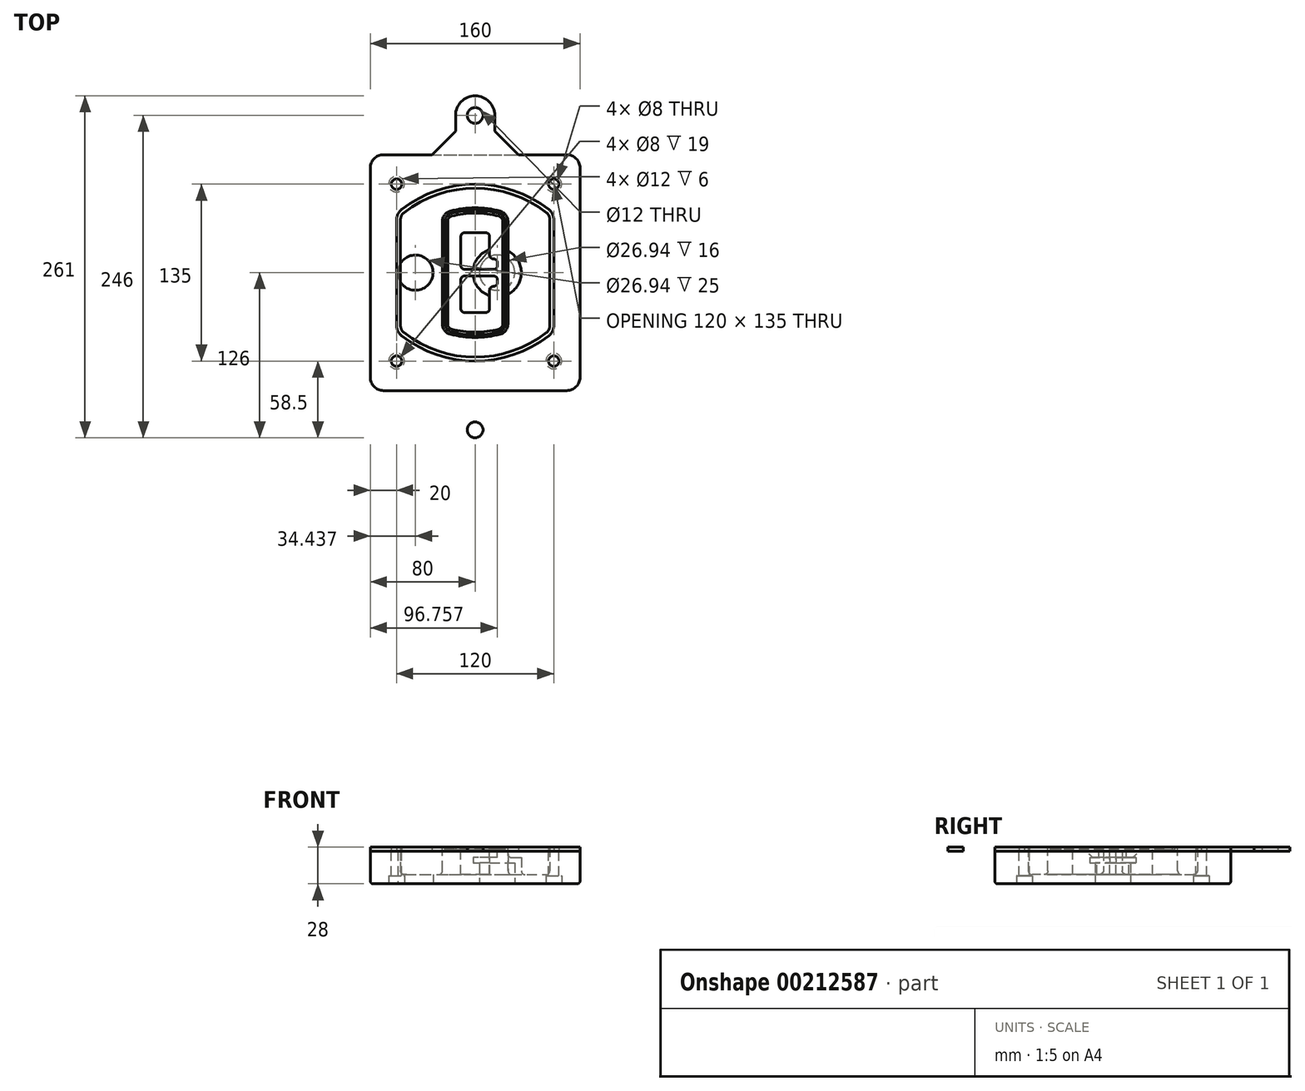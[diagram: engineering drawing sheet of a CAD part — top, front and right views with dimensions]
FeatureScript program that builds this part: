
annotation { "Feature Type Name" : "Feature", "Feature Type Description" : "" }
export const myFeature = defineFeature(function(context is Context, id is Id, definition is map)
    precondition{}
    {
        {
            var Q0;
            Q0=qCreatedBy(makeId("Top.planeOp"),FACE);
            var sketch = newSketch(context, id + "F0", { "sketchPlane" : qUnion([Q0])});
            skPoint(sketch, "E0.rect.middle", {"position": v(0, 0) * mm});
            skLineSegment(sketch, "E1.bottom", {"start": v(-70, -90) * mm, "end": v(70, -90) * mm});
            skLineSegment(sketch, "E1.top", {"start": v(-70, 90) * mm, "end": v(70, 90) * mm});
            skLineSegment(sketch, "E1.left", {"start": v(-80, -80) * mm, "end": v(-80, 80) * mm});
            skLineSegment(sketch, "E1.right", {"start": v(80, -80) * mm, "end": v(80, 80) * mm});
            skLineSegment(sketch, "E2", {"start": v(-80, 90) * mm, "end": v(80, -90) * mm, "construction": true});
            skLineSegment(sketch, "E3", {"start": v(80, 90) * mm, "end": v(-80, -90) * mm, "construction": true});
            skCircle(sketch, "E4", {"center": v(-60, 67.5) * mm, "radius": 4 * mm});
            skCircle(sketch, "E5", {"center": v(60, 67.5) * mm, "radius": 4 * mm});
            skCircle(sketch, "E6", {"center": v(60, -67.5) * mm, "radius": 4 * mm});
            skCircle(sketch, "E7", {"center": v(-60, -67.5) * mm, "radius": 4 * mm});
            skLineSegment(sketch, "E8", {"start": v(-60, 67.5) * mm, "end": v(60, 67.5) * mm, "construction": true});
            skLineSegment(sketch, "E9", {"start": v(60, 67.5) * mm, "end": v(60, -67.5) * mm, "construction": true});
            skLineSegment(sketch, "E10", {"start": v(60, -67.5) * mm, "end": v(-60, -67.5) * mm, "construction": true});
            skLineSegment(sketch, "E11", {"start": v(-60, -67.5) * mm, "end": v(-60, 67.5) * mm, "construction": true});
            skLineSegment(sketch, "E12", {"start": v(-60, 40.3) * mm, "end": v(-60, -40.3) * mm});
            skLineSegment(sketch, "E13", {"start": v(60, 40.3) * mm, "end": v(60, -40.3) * mm});
            skArc(sketch, "E14", {"start": v(56.15, 48.18) * mm, "mid": v(0, 67.5) * mm, "end": v(-56.15, 48.18) * mm});
            skArc(sketch, "E15", {"start": v(-56.15, -48.18) * mm, "mid": v(0, -67.5) * mm, "end": v(56.15, -48.18) * mm});
            skLineSegment(sketch, "E16", {"start": v(-60, 0) * mm, "end": v(60, 0) * mm, "construction": true});
            skPoint(sketch, "E17.visualSharp", {"position": v(-60, -45) * mm});
            skArc(sketch, "E17.filletArc", {"start": v(-60, -40.3) * mm, "mid": v(-58.99, -44.68) * mm, "end": v(-56.15, -48.18) * mm});
            skPoint(sketch, "E18.visualSharp", {"position": v(-60, 45) * mm});
            skArc(sketch, "E18.filletArc", {"start": v(-56.15, 48.18) * mm, "mid": v(-58.99, 44.68) * mm, "end": v(-60, 40.3) * mm});
            skPoint(sketch, "E19.visualSharp", {"position": v(60, 45) * mm});
            skArc(sketch, "E19.filletArc", {"start": v(60, 40.3) * mm, "mid": v(58.99, 44.68) * mm, "end": v(56.15, 48.18) * mm});
            skPoint(sketch, "E20.visualSharp", {"position": v(60, -45) * mm});
            skArc(sketch, "E20.filletArc", {"start": v(56.15, -48.18) * mm, "mid": v(58.99, -44.68) * mm, "end": v(60, -40.3) * mm});
            skPoint(sketch, "E21.visualSharp", {"position": v(-80, 90) * mm});
            skArc(sketch, "E21.filletArc", {"start": v(-70, 90) * mm, "mid": v(-77.07, 87.07) * mm, "end": v(-80, 80) * mm});
            skPoint(sketch, "E22.visualSharp", {"position": v(80, 90) * mm});
            skArc(sketch, "E22.filletArc", {"start": v(80, 80) * mm, "mid": v(77.07, 87.07) * mm, "end": v(70, 90) * mm});
            skPoint(sketch, "E23.visualSharp", {"position": v(80, -90) * mm});
            skArc(sketch, "E23.filletArc", {"start": v(70, -90) * mm, "mid": v(77.07, -87.07) * mm, "end": v(80, -80) * mm});
            skPoint(sketch, "E24.visualSharp", {"position": v(-80, -90) * mm});
            skArc(sketch, "E24.filletArc", {"start": v(-80, -80) * mm, "mid": v(-77.07, -87.07) * mm, "end": v(-70, -90) * mm});
            skArc(sketch, "E25.0", {"start": v(57, 40.3) * mm, "mid": v(56.3, 43.36) * mm, "end": v(54.3, 45.81) * mm});
            skLineSegment(sketch, "E25.1", {"start": v(57, 40.3) * mm, "end": v(57, -40.3) * mm});
            skArc(sketch, "E25.2", {"start": v(54.3, -45.81) * mm, "mid": v(56.3, -43.36) * mm, "end": v(57, -40.3) * mm});
            skArc(sketch, "E25.3", {"start": v(-54.3, -45.81) * mm, "mid": v(0, -64.5) * mm, "end": v(54.3, -45.81) * mm});
            skArc(sketch, "E25.4", {"start": v(-57, -40.3) * mm, "mid": v(-56.3, -43.36) * mm, "end": v(-54.3, -45.81) * mm});
            skArc(sketch, "E25.5", {"start": v(54.3, 45.81) * mm, "mid": v(0, 64.5) * mm, "end": v(-54.3, 45.81) * mm});
            skLineSegment(sketch, "E25.6", {"start": v(-57, 40.3) * mm, "end": v(-57, -40.3) * mm});
            skArc(sketch, "E25.7", {"start": v(-54.3, 45.81) * mm, "mid": v(-56.3, 43.36) * mm, "end": v(-57, 40.3) * mm});
            skArc(sketch, "E26.0", {"start": v(-58.62, 51.33) * mm, "mid": v(-62.58, 46.43) * mm, "end": v(-64, 40.3) * mm});
            skArc(sketch, "E26.1", {"start": v(58.62, 51.33) * mm, "mid": v(0, 71.5) * mm, "end": v(-58.62, 51.33) * mm});
            skArc(sketch, "E26.2", {"start": v(64, 40.3) * mm, "mid": v(62.58, 46.43) * mm, "end": v(58.62, 51.33) * mm});
            skLineSegment(sketch, "E26.3", {"start": v(64, 40.3) * mm, "end": v(64, -40.3) * mm});
            skArc(sketch, "E26.4", {"start": v(58.62, -51.33) * mm, "mid": v(62.58, -46.43) * mm, "end": v(64, -40.3) * mm});
            skLineSegment(sketch, "E26.5", {"start": v(-64, 40.3) * mm, "end": v(-64, -40.3) * mm});
            skArc(sketch, "E26.6", {"start": v(-58.62, -51.33) * mm, "mid": v(0, -71.5) * mm, "end": v(58.62, -51.33) * mm});
            skArc(sketch, "E26.7", {"start": v(-64, -40.3) * mm, "mid": v(-62.58, -46.43) * mm, "end": v(-58.62, -51.33) * mm});
            skSolve(sketch);
        }
        {
            var Q0;
            Q0=makeQuery(id+"F0.imprint","IMPRINT",FACE,{"disambiguationData":[TD([[makeQuery(id+"F0.imprint","IMPRINT",EDGE,{"derivedFrom":sQuery(id+"F0.wireOp",EDGE,"E1.bottom")}),1.0]])]});
            var Q1;
            Q1=makeQuery(id+"F0.imprint","IMPRINT",FACE,{"disambiguationData":[TD([[makeQuery(id+"F0.imprint","IMPRINT",EDGE,{"derivedFrom":sQuery(id+"F0.wireOp",EDGE,"E12")}),1.0]])]});
            var Q2;
            Q2=makeQuery(id+"F0.imprint","IMPRINT",FACE,{"disambiguationData":[TD([[makeQuery(id+"F0.imprint","IMPRINT",EDGE,{"derivedFrom":sQuery(id+"F0.wireOp",EDGE,"E25.0")}),1.0]])]});
            var Q3;
            Q3=makeQuery(id+"F0.imprint","IMPRINT",FACE,{"disambiguationData":[TD([[makeQuery(id+"F0.imprint","IMPRINT",EDGE,{"derivedFrom":sQuery(id+"F0.wireOp",EDGE,"E12")}),-1.0]])]});
            extrude(context, id + "F1", {"entities" : qUnion([Q0, Q1, Q2, Q3]), "oppositeDirection" : true, "depth" : 25 * mm});
        }
        {
            var Q0;
            Q0=makeQuery(id+"F0.imprint","IMPRINT",FACE,{"disambiguationData":[TD([[makeQuery(id+"F0.imprint","IMPRINT",EDGE,{"derivedFrom":sQuery(id+"F0.wireOp",EDGE,"E12")}),1.0]])]});
            extrude(context, id + "F2", {"entities" : qUnion([Q0]), "operationType" : NewBodyOperationType.ADD, "depth" : 3 * mm});
        }
        {
            var Q0;
            Q0=makeQuery(id+"F0.imprint","IMPRINT",FACE,{"disambiguationData":[TD([[makeQuery(id+"F0.imprint","IMPRINT",EDGE,{"derivedFrom":sQuery(id+"F0.wireOp",EDGE,"E25.0")}),1.0]])]});
            extrude(context, id + "F3", {"entities" : qUnion([Q0]), "operationType" : NewBodyOperationType.REMOVE, "oppositeDirection" : true, "depth" : 18 * mm});
        }
        {
            var Q0;
            Q0=makeQuery(id+"F2.opExtrude","CAP_FACE",FACE,{"disambiguationData":[OSD([sQuery(id+"F0.wireOp",EDGE,"E12"),sQuery(id+"F0.wireOp",EDGE,"E13"),sQuery(id+"F0.wireOp",EDGE,"E14"),sQuery(id+"F0.wireOp",EDGE,"E15"),sQuery(id+"F0.wireOp",EDGE,"E17.filletArc"),sQuery(id+"F0.wireOp",EDGE,"E18.filletArc"),sQuery(id+"F0.wireOp",EDGE,"E19.filletArc"),sQuery(id+"F0.wireOp",EDGE,"E20.filletArc"),sQuery(id+"F0.wireOp",EDGE,"E25.0"),sQuery(id+"F0.wireOp",EDGE,"E25.1"),sQuery(id+"F0.wireOp",EDGE,"E25.2"),sQuery(id+"F0.wireOp",EDGE,"E25.3"),sQuery(id+"F0.wireOp",EDGE,"E25.4"),sQuery(id+"F0.wireOp",EDGE,"E25.5"),sQuery(id+"F0.wireOp",EDGE,"E25.6"),sQuery(id+"F0.wireOp",EDGE,"E25.7")])],"isStart":false});
            var sketch = newSketch(context, id + "F4", { "sketchPlane" : qUnion([Q0])});
            skArc(sketch, "E27.0", {"start": v(-19.08, -46.97) * mm, "mid": v(0, -49.5) * mm, "end": v(19.08, -46.97) * mm});
            skArc(sketch, "E28.0", {"start": v(19.08, 46.97) * mm, "mid": v(0, 49.5) * mm, "end": v(-19.08, 46.97) * mm});
            skLineSegment(sketch, "E29", {"start": v(-25, 39.25) * mm, "end": v(-25, -39.25) * mm});
            skLineSegment(sketch, "E30", {"start": v(25, 39.25) * mm, "end": v(25, -39.25) * mm});
            skLineSegment(sketch, "E31", {"start": v(-25, 45.1) * mm, "end": v(25, 45.1) * mm, "construction": true});
            skLineSegment(sketch, "E32", {"start": v(-25, -45.1) * mm, "end": v(25, -45.1) * mm, "construction": true});
            skPoint(sketch, "E33.visualSharp", {"position": v(-25, 45.1) * mm});
            skArc(sketch, "E33.filletArc", {"start": v(-19.08, 46.97) * mm, "mid": v(-23.35, 44.11) * mm, "end": v(-25, 39.25) * mm});
            skPoint(sketch, "E34.visualSharp", {"position": v(25, 45.1) * mm});
            skArc(sketch, "E34.filletArc", {"start": v(25, 39.25) * mm, "mid": v(23.35, 44.11) * mm, "end": v(19.08, 46.97) * mm});
            skPoint(sketch, "E35.visualSharp", {"position": v(25, -45.1) * mm});
            skArc(sketch, "E35.filletArc", {"start": v(19.08, -46.97) * mm, "mid": v(23.35, -44.11) * mm, "end": v(25, -39.25) * mm});
            skPoint(sketch, "E36.visualSharp", {"position": v(-25, -45.1) * mm});
            skArc(sketch, "E36.filletArc", {"start": v(-25, -39.25) * mm, "mid": v(-23.35, -44.11) * mm, "end": v(-19.08, -46.97) * mm});
            skArc(sketch, "E37.0", {"start": v(54.3, 45.81) * mm, "mid": v(0, 64.5) * mm, "end": v(-54.3, 45.81) * mm});
            skArc(sketch, "E37.1", {"start": v(-54.3, 45.81) * mm, "mid": v(-56.3, 43.36) * mm, "end": v(-57, 40.3) * mm});
            skLineSegment(sketch, "E37.2", {"start": v(-57, 40.3) * mm, "end": v(-57, -40.3) * mm});
            skArc(sketch, "E37.3", {"start": v(-57, -40.3) * mm, "mid": v(-56.3, -43.36) * mm, "end": v(-54.3, -45.81) * mm});
            skArc(sketch, "E37.4", {"start": v(-54.3, -45.81) * mm, "mid": v(0, -64.5) * mm, "end": v(54.3, -45.81) * mm});
            skArc(sketch, "E37.5", {"start": v(54.3, -45.81) * mm, "mid": v(56.3, -43.36) * mm, "end": v(57, -40.3) * mm});
            skLineSegment(sketch, "E37.6", {"start": v(57, 40.3) * mm, "end": v(57, -40.3) * mm});
            skArc(sketch, "E37.7", {"start": v(57, 40.3) * mm, "mid": v(56.3, 43.36) * mm, "end": v(54.3, 45.81) * mm});
            skLineSegment(sketch, "E38.0", {"start": v(23, 39.25) * mm, "end": v(23, -39.25) * mm});
            skArc(sketch, "E38.1", {"start": v(18.56, -45.04) * mm, "mid": v(21.76, -42.9) * mm, "end": v(23, -39.25) * mm});
            skArc(sketch, "E38.2", {"start": v(-18.56, -45.04) * mm, "mid": v(0, -47.5) * mm, "end": v(18.56, -45.04) * mm});
            skArc(sketch, "E38.3", {"start": v(-23, -39.25) * mm, "mid": v(-21.76, -42.9) * mm, "end": v(-18.56, -45.04) * mm});
            skLineSegment(sketch, "E38.4", {"start": v(-23, 39.25) * mm, "end": v(-23, -39.25) * mm});
            skArc(sketch, "E38.5", {"start": v(23, 39.25) * mm, "mid": v(21.76, 42.9) * mm, "end": v(18.56, 45.04) * mm});
            skArc(sketch, "E38.6", {"start": v(-18.56, 45.04) * mm, "mid": v(-21.76, 42.9) * mm, "end": v(-23, 39.25) * mm});
            skArc(sketch, "E38.7", {"start": v(18.56, 45.04) * mm, "mid": v(0, 47.5) * mm, "end": v(-18.56, 45.04) * mm});
            skArc(sketch, "E39.0", {"start": v(21, 39.25) * mm, "mid": v(20.18, 41.68) * mm, "end": v(18.04, 43.1) * mm});
            skLineSegment(sketch, "E39.1", {"start": v(21, 39.25) * mm, "end": v(21, -39.25) * mm});
            skArc(sketch, "E39.2", {"start": v(18.04, -43.1) * mm, "mid": v(20.18, -41.68) * mm, "end": v(21, -39.25) * mm});
            skArc(sketch, "E39.3", {"start": v(-18.04, -43.1) * mm, "mid": v(0, -45.5) * mm, "end": v(18.04, -43.1) * mm});
            skArc(sketch, "E39.4", {"start": v(-21, -39.25) * mm, "mid": v(-20.18, -41.68) * mm, "end": v(-18.04, -43.1) * mm});
            skArc(sketch, "E39.5", {"start": v(18.04, 43.1) * mm, "mid": v(0, 45.5) * mm, "end": v(-18.04, 43.1) * mm});
            skLineSegment(sketch, "E39.6", {"start": v(-21, 39.25) * mm, "end": v(-21, -39.25) * mm});
            skArc(sketch, "E39.7", {"start": v(-18.04, 43.1) * mm, "mid": v(-20.18, 41.68) * mm, "end": v(-21, 39.25) * mm});
            skLineSegment(sketch, "E40", {"start": v(-25, 0) * mm, "end": v(25, 0) * mm, "construction": true});
            skLineSegment(sketch, "E41", {"start": v(-11, 5.5) * mm, "end": v(-11, 27.5) * mm});
            skLineSegment(sketch, "E42", {"start": v(-8, 30.5) * mm, "end": v(8, 30.5) * mm});
            skLineSegment(sketch, "E43", {"start": v(11, 27.5) * mm, "end": v(11, 13.5) * mm});
            skLineSegment(sketch, "E44", {"start": v(14, 10.5) * mm, "end": v(14, 10.5) * mm});
            skLineSegment(sketch, "E45", {"start": v(17, 7.5) * mm, "end": v(17, 5.5) * mm});
            skLineSegment(sketch, "E46", {"start": v(14, 2.5) * mm, "end": v(-8, 2.5) * mm});
            skPoint(sketch, "E47.visualSharp", {"position": v(-11, 30.5) * mm});
            skArc(sketch, "E47.filletArc", {"start": v(-8, 30.5) * mm, "mid": v(-10.12, 29.62) * mm, "end": v(-11, 27.5) * mm});
            skPoint(sketch, "E48.visualSharp", {"position": v(11, 30.5) * mm});
            skArc(sketch, "E48.filletArc", {"start": v(11, 27.5) * mm, "mid": v(10.12, 29.62) * mm, "end": v(8, 30.5) * mm});
            skPoint(sketch, "E49.visualSharp", {"position": v(11, 10.5) * mm});
            skArc(sketch, "E49.filletArc", {"start": v(11, 13.5) * mm, "mid": v(11.88, 11.38) * mm, "end": v(14, 10.5) * mm});
            skPoint(sketch, "E50.visualSharp", {"position": v(17, 10.5) * mm});
            skArc(sketch, "E50.filletArc", {"start": v(17, 7.5) * mm, "mid": v(16.12, 9.62) * mm, "end": v(14, 10.5) * mm});
            skPoint(sketch, "E51.visualSharp", {"position": v(17, 2.5) * mm});
            skArc(sketch, "E51.filletArc", {"start": v(14, 2.5) * mm, "mid": v(16.12, 3.38) * mm, "end": v(17, 5.5) * mm});
            skPoint(sketch, "E52.visualSharp", {"position": v(-11, 2.5) * mm});
            skArc(sketch, "E52.filletArc", {"start": v(-11, 5.5) * mm, "mid": v(-10.12, 3.38) * mm, "end": v(-8, 2.5) * mm});
            skLineSegment(sketch, "E53.0.MirrorCS", {"start": v(14, -2.5) * mm, "end": v(-8, -2.5) * mm});
            skArc(sketch, "E54.0.MirrorCS", {"start": v(-11, -5.5) * mm, "mid": v(-10.12, -3.38) * mm, "end": v(-8, -2.5) * mm});
            skLineSegment(sketch, "E55.0.MirrorCS", {"start": v(-11, -5.5) * mm, "end": v(-11, -27.5) * mm});
            skArc(sketch, "E56.0.MirrorCS", {"start": v(-8, -30.5) * mm, "mid": v(-10.12, -29.62) * mm, "end": v(-11, -27.5) * mm});
            skLineSegment(sketch, "E57.0.MirrorCS", {"start": v(-8, -30.5) * mm, "end": v(8, -30.5) * mm});
            skArc(sketch, "E58.0.MirrorCS", {"start": v(11, -27.5) * mm, "mid": v(10.12, -29.62) * mm, "end": v(8, -30.5) * mm});
            skLineSegment(sketch, "E59.0.MirrorCS", {"start": v(11, -27.5) * mm, "end": v(11, -13.5) * mm});
            skArc(sketch, "E60.0.MirrorCS", {"start": v(11, -13.5) * mm, "mid": v(11.88, -11.38) * mm, "end": v(14, -10.5) * mm});
            skArc(sketch, "E61.0.MirrorCS", {"start": v(17, -7.5) * mm, "mid": v(16.12, -9.62) * mm, "end": v(14, -10.5) * mm});
            skLineSegment(sketch, "E62.0.MirrorCS", {"start": v(17, -7.5) * mm, "end": v(17, -5.5) * mm});
            skArc(sketch, "E63.0.MirrorCS", {"start": v(14, -2.5) * mm, "mid": v(16.12, -3.38) * mm, "end": v(17, -5.5) * mm});
            skSolve(sketch);
        }
        {
            var Q0;
            Q0=makeQuery(id+"F4.imprint","IMPRINT",FACE,{"disambiguationData":[TD([[makeQuery(id+"F4.imprint","IMPRINT",EDGE,{"derivedFrom":sQuery(id+"F4.wireOp",EDGE,"E27.0")}),1.0]])]});
            var Q1;
            Q1=makeQuery(id+"F4.imprint","IMPRINT",FACE,{"disambiguationData":[TD([[makeQuery(id+"F4.imprint","IMPRINT",EDGE,{"derivedFrom":sQuery(id+"F4.wireOp",EDGE,"E38.0")}),-1.0]])]});
            var Q2;
            Q2=makeQuery(id+"F4.imprint","IMPRINT",FACE,{"disambiguationData":[TD([[makeQuery(id+"F4.imprint","IMPRINT",EDGE,{"derivedFrom":sQuery(id+"F4.wireOp",EDGE,"E39.0")}),1.0]])]});
            extrude(context, id + "F5", {"entities" : qUnion([Q0, Q1, Q2]), "operationType" : NewBodyOperationType.ADD, "endBound" : BoundingType.UP_TO_NEXT, "oppositeDirection" : true, "depth" : 25 * mm});
        }
        {
            var Q0;
            Q0=makeQuery(id+"F4.imprint","IMPRINT",FACE,{"disambiguationData":[TD([[makeQuery(id+"F4.imprint","IMPRINT",EDGE,{"derivedFrom":sQuery(id+"F4.wireOp",EDGE,"E38.0")}),-1.0]])]});
            extrude(context, id + "F6", {"entities" : qUnion([Q0]), "operationType" : NewBodyOperationType.REMOVE, "oppositeDirection" : true, "depth" : 2 * mm});
        }
        {
            var Q0;
            Q0=makeQuery(id+"F1.opExtrude","CAP_FACE",FACE,{"disambiguationData":[OSD([sQuery(id+"F0.wireOp",EDGE,"E1.bottom"),sQuery(id+"F0.wireOp",EDGE,"E1.top"),sQuery(id+"F0.wireOp",EDGE,"E1.left"),sQuery(id+"F0.wireOp",EDGE,"E1.right"),sQuery(id+"F0.wireOp",EDGE,"E4"),sQuery(id+"F0.wireOp",EDGE,"E5"),sQuery(id+"F0.wireOp",EDGE,"E6"),sQuery(id+"F0.wireOp",EDGE,"E7"),sQuery(id+"F0.wireOp",EDGE,"E21.filletArc"),sQuery(id+"F0.wireOp",EDGE,"E22.filletArc"),sQuery(id+"F0.wireOp",EDGE,"E23.filletArc"),sQuery(id+"F0.wireOp",EDGE,"E24.filletArc")])],"isStart":false});
            var sketch = newSketch(context, id + "F7", { "sketchPlane" : qUnion([Q0])});
            skCircle(sketch, "E64", {"center": v(16.76, 0) * mm, "radius": 13.47 * mm});
            skCircle(sketch, "E65", {"center": v(-45.56, 0) * mm, "radius": 13.47 * mm});
            skLineSegment(sketch, "E66", {"start": v(80, 0) * mm, "end": v(-80, 0) * mm});
            skCircle(sketch, "E67", {"center": v(16.76, 0) * mm, "radius": 18.47 * mm});
            skCircle(sketch, "E68", {"center": v(60, -67.5) * mm, "radius": 6 * mm});
            skCircle(sketch, "E69", {"center": v(-60, -67.5) * mm, "radius": 6 * mm});
            skCircle(sketch, "E70", {"center": v(-60, 67.5) * mm, "radius": 6 * mm});
            skCircle(sketch, "E71", {"center": v(60, 67.5) * mm, "radius": 6 * mm});
            skSolve(sketch);
        }
        {
            var Q0;
            {var subQ1=sQuery(id+"F7.wireOp",EDGE,"E66");var subQ4=sQuery(id+"F7.wireOp",EDGE,"E64");var subQ6=makeQuery(id+"F7.imprint","INTERSECT",VERTEX,{"disambiguationData":[OD(0.0)],"derivedFrom":[subQ4,subQ1]});Q0=makeQuery(id+"F7.imprint","IMPRINT",FACE,{"disambiguationData":[TD([[makeQuery(id+"F7.imprint","IMPRINT",EDGE,{"disambiguationData":[TD([[subQ6,-1.0]])],"derivedFrom":subQ4}),-1.0]])]});}
            var Q1;
            {var subQ0=sQuery(id+"F7.wireOp",EDGE,"E66");var subQ1=sQuery(id+"F7.wireOp",EDGE,"E64");var subQ3=makeQuery(id+"F7.imprint","INTERSECT",VERTEX,{"disambiguationData":[OD(0.0)],"derivedFrom":[subQ1,subQ0]});Q1=makeQuery(id+"F7.imprint","IMPRINT",FACE,{"disambiguationData":[TD([[makeQuery(id+"F7.imprint","IMPRINT",EDGE,{"disambiguationData":[TD([[subQ3,-1.0]])],"derivedFrom":subQ1}),1.0]])]});}
            var Q2;
            {var subQ0=sQuery(id+"F7.wireOp",EDGE,"E66");var subQ1=sQuery(id+"F7.wireOp",EDGE,"E64");var subQ3=makeQuery(id+"F7.imprint","INTERSECT",VERTEX,{"disambiguationData":[OD(0.0)],"derivedFrom":[subQ1,subQ0]});Q2=makeQuery(id+"F7.imprint","IMPRINT",FACE,{"disambiguationData":[TD([[makeQuery(id+"F7.imprint","IMPRINT",EDGE,{"disambiguationData":[TD([[subQ3,1.0]])],"derivedFrom":subQ1}),1.0]])]});}
            var Q3;
            {var subQ1=sQuery(id+"F7.wireOp",EDGE,"E66");var subQ4=sQuery(id+"F7.wireOp",EDGE,"E64");var subQ6=makeQuery(id+"F7.imprint","INTERSECT",VERTEX,{"disambiguationData":[OD(0.0)],"derivedFrom":[subQ4,subQ1]});Q3=makeQuery(id+"F7.imprint","IMPRINT",FACE,{"disambiguationData":[TD([[makeQuery(id+"F7.imprint","IMPRINT",EDGE,{"disambiguationData":[TD([[subQ6,1.0]])],"derivedFrom":subQ4}),-1.0]])]});}
            extrude(context, id + "F8", {"entities" : qUnion([Q0, Q1, Q2, Q3]), "operationType" : NewBodyOperationType.ADD, "oppositeDirection" : true, "depth" : 20 * mm});
        }
        {
            var Q0;
            {var subQ0=sQuery(id+"F7.wireOp",EDGE,"E66");var subQ1=sQuery(id+"F7.wireOp",EDGE,"E64");var subQ3=makeQuery(id+"F7.imprint","INTERSECT",VERTEX,{"disambiguationData":[OD(0.0)],"derivedFrom":[subQ1,subQ0]});Q0=makeQuery(id+"F7.imprint","IMPRINT",FACE,{"disambiguationData":[TD([[makeQuery(id+"F7.imprint","IMPRINT",EDGE,{"disambiguationData":[TD([[subQ3,-1.0]])],"derivedFrom":subQ1}),1.0]])]});}
            var Q1;
            {var subQ0=sQuery(id+"F7.wireOp",EDGE,"E66");var subQ1=sQuery(id+"F7.wireOp",EDGE,"E64");var subQ3=makeQuery(id+"F7.imprint","INTERSECT",VERTEX,{"disambiguationData":[OD(0.0)],"derivedFrom":[subQ1,subQ0]});Q1=makeQuery(id+"F7.imprint","IMPRINT",FACE,{"disambiguationData":[TD([[makeQuery(id+"F7.imprint","IMPRINT",EDGE,{"disambiguationData":[TD([[subQ3,1.0]])],"derivedFrom":subQ1}),1.0]])]});}
            extrude(context, id + "F9", {"entities" : qUnion([Q0, Q1]), "operationType" : NewBodyOperationType.REMOVE, "oppositeDirection" : true, "depth" : 16 * mm});
        }
        {
            var Q0;
            {var subQ0=sQuery(id+"F7.wireOp",EDGE,"E66");var subQ1=sQuery(id+"F7.wireOp",EDGE,"E65");var subQ3=makeQuery(id+"F7.imprint","INTERSECT",VERTEX,{"disambiguationData":[OD(0.0)],"derivedFrom":[subQ1,subQ0]});Q0=makeQuery(id+"F7.imprint","IMPRINT",FACE,{"disambiguationData":[TD([[makeQuery(id+"F7.imprint","IMPRINT",EDGE,{"disambiguationData":[TD([[subQ3,-1.0]])],"derivedFrom":subQ1}),1.0]])]});}
            var Q1;
            {var subQ0=sQuery(id+"F7.wireOp",EDGE,"E66");var subQ1=sQuery(id+"F7.wireOp",EDGE,"E65");var subQ3=makeQuery(id+"F7.imprint","INTERSECT",VERTEX,{"disambiguationData":[OD(0.0)],"derivedFrom":[subQ1,subQ0]});Q1=makeQuery(id+"F7.imprint","IMPRINT",FACE,{"disambiguationData":[TD([[makeQuery(id+"F7.imprint","IMPRINT",EDGE,{"disambiguationData":[TD([[subQ3,1.0]])],"derivedFrom":subQ1}),1.0]])]});}
            extrude(context, id + "F10", {"entities" : qUnion([Q0, Q1]), "operationType" : NewBodyOperationType.REMOVE, "oppositeDirection" : true, "depth" : 25 * mm});
        }
        {
            var Q0;
            Q0=makeQuery(id+"F7.imprint","IMPRINT",FACE,{"disambiguationData":[TD([[makeQuery(id+"F7.imprint","IMPRINT",EDGE,{"derivedFrom":sQuery(id+"F7.wireOp",EDGE,"E68")}),1.0]])]});
            var Q1;
            Q1=makeQuery(id+"F7.imprint","IMPRINT",FACE,{"disambiguationData":[TD([[makeQuery(id+"F7.imprint","IMPRINT",EDGE,{"derivedFrom":makeQuery(id+"F1.opExtrude","CAP_EDGE",EDGE,{"disambiguationData":[OSD([sQuery(id+"F0.wireOp",EDGE,"E5")])],"isStart":false})}),-1.0]])]});
            var Q2;
            Q2=makeQuery(id+"F7.imprint","IMPRINT",FACE,{"disambiguationData":[TD([[makeQuery(id+"F7.imprint","IMPRINT",EDGE,{"derivedFrom":sQuery(id+"F7.wireOp",EDGE,"E69")}),1.0]])]});
            var Q3;
            Q3=makeQuery(id+"F7.imprint","IMPRINT",FACE,{"disambiguationData":[TD([[makeQuery(id+"F7.imprint","IMPRINT",EDGE,{"derivedFrom":makeQuery(id+"F1.opExtrude","CAP_EDGE",EDGE,{"disambiguationData":[OSD([sQuery(id+"F0.wireOp",EDGE,"E4")])],"isStart":false})}),-1.0]])]});
            var Q4;
            Q4=makeQuery(id+"F7.imprint","IMPRINT",FACE,{"disambiguationData":[TD([[makeQuery(id+"F7.imprint","IMPRINT",EDGE,{"derivedFrom":sQuery(id+"F7.wireOp",EDGE,"E70")}),1.0]])]});
            var Q5;
            Q5=makeQuery(id+"F7.imprint","IMPRINT",FACE,{"disambiguationData":[TD([[makeQuery(id+"F7.imprint","IMPRINT",EDGE,{"derivedFrom":makeQuery(id+"F1.opExtrude","CAP_EDGE",EDGE,{"disambiguationData":[OSD([sQuery(id+"F0.wireOp",EDGE,"E7")])],"isStart":false})}),-1.0]])]});
            var Q6;
            Q6=makeQuery(id+"F7.imprint","IMPRINT",FACE,{"disambiguationData":[TD([[makeQuery(id+"F7.imprint","IMPRINT",EDGE,{"derivedFrom":sQuery(id+"F7.wireOp",EDGE,"E71")}),1.0]])]});
            var Q7;
            Q7=makeQuery(id+"F7.imprint","IMPRINT",FACE,{"disambiguationData":[TD([[makeQuery(id+"F7.imprint","IMPRINT",EDGE,{"derivedFrom":makeQuery(id+"F1.opExtrude","CAP_EDGE",EDGE,{"disambiguationData":[OSD([sQuery(id+"F0.wireOp",EDGE,"E6")])],"isStart":false})}),-1.0]])]});
            extrude(context, id + "F11", {"entities" : qUnion([Q0, Q1, Q2, Q3, Q4, Q5, Q6, Q7]), "operationType" : NewBodyOperationType.REMOVE, "oppositeDirection" : true, "depth" : 6 * mm});
        }
        {
            var Q0;
            Q0=makeQuery(id+"F9.boolean.opBoolean","COPY",FACE,{"derivedFrom":makeQuery(id+"F9.opExtrude","CAP_FACE",FACE,{"disambiguationData":[OSD([sQuery(id+"F7.wireOp",EDGE,"E64")])],"isStart":false})});
            var sketch = newSketch(context, id + "F12", { "sketchPlane" : qUnion([Q0])});
            skArc(sketch, "E72.0", {"start": v(11, 17.55) * mm, "mid": v(2.57, 11.82) * mm, "end": v(-1.54, 2.5) * mm});
            skArc(sketch, "E72.1", {"start": v(-1.54, -2.5) * mm, "mid": v(2.57, -11.82) * mm, "end": v(11, -17.55) * mm});
            skLineSegment(sketch, "E73", {"start": v(-1.54, -2.5) * mm, "end": v(14, -2.5) * mm});
            skLineSegment(sketch, "E74.0", {"start": v(14, 2.5) * mm, "end": v(-1.54, 2.5) * mm});
            skArc(sketch, "E74.1", {"start": v(14, 2.5) * mm, "mid": v(16.12, 3.38) * mm, "end": v(17, 5.5) * mm});
            skLineSegment(sketch, "E74.2", {"start": v(17, 7.5) * mm, "end": v(17, 5.5) * mm});
            skArc(sketch, "E74.3", {"start": v(17, 7.5) * mm, "mid": v(16.12, 9.62) * mm, "end": v(14, 10.5) * mm});
            skArc(sketch, "E74.4", {"start": v(11, 13.5) * mm, "mid": v(11.88, 11.38) * mm, "end": v(14, 10.5) * mm});
            skLineSegment(sketch, "E74.5", {"start": v(11, 17.55) * mm, "end": v(11, 13.5) * mm});
            skLineSegment(sketch, "E74.7", {"start": v(14, -2.5) * mm, "end": v(-1.54, -2.5) * mm});
            skArc(sketch, "E74.8", {"start": v(14, -2.5) * mm, "mid": v(16.12, -3.38) * mm, "end": v(17, -5.5) * mm});
            skLineSegment(sketch, "E74.9", {"start": v(17, -7.5) * mm, "end": v(17, -5.5) * mm});
            skArc(sketch, "E74.10", {"start": v(17, -7.5) * mm, "mid": v(16.12, -9.62) * mm, "end": v(14, -10.5) * mm});
            skArc(sketch, "E74.11", {"start": v(11, -13.5) * mm, "mid": v(11.88, -11.38) * mm, "end": v(14, -10.5) * mm});
            skLineSegment(sketch, "E74.12", {"start": v(11, -17.55) * mm, "end": v(11, -13.5) * mm});
            skPoint(sketch, "E75.orphan", {"position": v(11, -27.5) * mm});
            skPoint(sketch, "E76.orphan", {"position": v(-8, -2.5) * mm});
            skPoint(sketch, "E77.orphan", {"position": v(-8, 2.5) * mm});
            skPoint(sketch, "E78.orphan", {"position": v(11, 27.5) * mm});
            skSolve(sketch);
        }
        {
            var Q0;
            {var subQ7=sQuery(id+"F12.wireOp",EDGE,"E72.0");var subQ14=sQuery(id+"F12.wireOp",EDGE,"E72.1");var subQ16=sQuery(id+"F12.wireOp",EDGE,"E74.1");var subQ18=sQuery(id+"F12.wireOp",EDGE,"E74.8");Q0=qUnion([makeQuery(id+"F12.imprint","IMPRINT",FACE,{"disambiguationData":[TD([[makeQuery(id+"F12.imprint","IMPRINT",EDGE,{"derivedFrom":subQ7}),1.0]])]}),makeQuery(id+"F12.imprint","IMPRINT",FACE,{"disambiguationData":[TD([[makeQuery(id+"F12.imprint","IMPRINT",EDGE,{"derivedFrom":subQ14}),1.0]])]}),makeQuery(id+"F12.imprint","IMPRINT",FACE,{"disambiguationData":[TD([[makeQuery(id+"F12.imprint","IMPRINT",EDGE,{"derivedFrom":subQ16}),1.0]])]}),makeQuery(id+"F12.imprint","IMPRINT",FACE,{"disambiguationData":[TD([[makeQuery(id+"F12.imprint","IMPRINT",EDGE,{"derivedFrom":subQ18}),-1.0]])]})]);}
            var Q1;
            Q1=makeQuery(id+"F5.boolean.opBoolean","SPLIT",FACE,{"disambiguationData":[TD([makeQuery(id+"F5.opExtrude","SWEPT_FACE",FACE,{"disambiguationData":[OSD([sQuery(id+"F4.wireOp",EDGE,"E41")])]})])],"derivedFrom":makeQuery(id+"F3.boolean.opBoolean","COPY",FACE,{"derivedFrom":makeQuery(id+"F3.opExtrude","CAP_FACE",FACE,{"disambiguationData":[OSD([sQuery(id+"F0.wireOp",EDGE,"E25.0"),sQuery(id+"F0.wireOp",EDGE,"E25.1"),sQuery(id+"F0.wireOp",EDGE,"E25.2"),sQuery(id+"F0.wireOp",EDGE,"E25.3"),sQuery(id+"F0.wireOp",EDGE,"E25.4"),sQuery(id+"F0.wireOp",EDGE,"E25.5"),sQuery(id+"F0.wireOp",EDGE,"E25.6"),sQuery(id+"F0.wireOp",EDGE,"E25.7")])],"isStart":false})})});
            extrude(context, id + "F13", {"entities" : qUnion([Q0]), "operationType" : NewBodyOperationType.REMOVE, "endBound" : BoundingType.UP_TO_SURFACE, "endBoundEntityFace" : qUnion([Q1]), "depth" : 25 * mm});
        }
        {
            var Q0;
            Q0=makeQuery(id+"F3.boolean.opBoolean","COPY",EDGE,{"derivedFrom":makeQuery(id+"F3.opExtrude","CAP_EDGE",EDGE,{"disambiguationData":[OSD([sQuery(id+"F0.wireOp",EDGE,"E25.6")])],"isStart":false})});
            var Q1;
            Q1=makeQuery(id+"F8.boolean.opBoolean","INTERSECT",EDGE,{"derivedFrom":[makeQuery(id+"F5.opExtrude","SWEPT_FACE",FACE,{"disambiguationData":[OSD([sQuery(id+"F4.wireOp",EDGE,"E30")])]}),makeQuery(id+"F8.opExtrude","CAP_FACE",FACE,{"disambiguationData":[OSD([sQuery(id+"F7.wireOp",EDGE,"E67")])],"isStart":false})]});
            var Q2;
            Q2=makeQuery(id+"F8.boolean.opBoolean","INTERSECT",EDGE,{"disambiguationData":[OD(1.0)],"derivedFrom":[makeQuery(id+"F5.opExtrude","SWEPT_FACE",FACE,{"disambiguationData":[OSD([sQuery(id+"F4.wireOp",EDGE,"E30")])]}),makeQuery(id+"F8.opExtrude","SWEPT_FACE",FACE,{"disambiguationData":[OSD([sQuery(id+"F7.wireOp",EDGE,"E67")])]})]});
            var Q3;
            {var subQ0=sQuery(id+"F4.wireOp",EDGE,"E30");Q3=makeQuery(id+"F8.boolean.opBoolean","SPLIT",EDGE,{"disambiguationData":[TD([makeQuery(id+"F5.opExtrude","SWEPT_FACE",FACE,{"disambiguationData":[OSD([sQuery(id+"F4.wireOp",EDGE,"E35.filletArc")])]})])],"derivedFrom":makeQuery(id+"F5.opExtrude","CAP_EDGE",EDGE,{"disambiguationData":[OSD([subQ0])],"isStart":false})});}
            var Q4;
            {var subQ0=sQuery(id+"F0.wireOp",EDGE,"E25.7");var subQ1=sQuery(id+"F0.wireOp",EDGE,"E25.1");var subQ2=sQuery(id+"F0.wireOp",EDGE,"E25.6");var subQ3=sQuery(id+"F0.wireOp",EDGE,"E25.5");var subQ4=sQuery(id+"F0.wireOp",EDGE,"E25.4");var subQ5=sQuery(id+"F0.wireOp",EDGE,"E25.0");var subQ6=sQuery(id+"F0.wireOp",EDGE,"E25.2");var subQ7=sQuery(id+"F0.wireOp",EDGE,"E25.3");Q4=makeQuery(id+"F8.boolean.opBoolean","INTERSECT",EDGE,{"derivedFrom":[makeQuery(id+"F5.boolean.opBoolean","SPLIT",FACE,{"disambiguationData":[TD([makeQuery(id+"F2.opExtrude","SWEPT_FACE",FACE,{"disambiguationData":[OSD([subQ5])]})])],"derivedFrom":makeQuery(id+"F3.boolean.opBoolean","COPY",FACE,{"derivedFrom":makeQuery(id+"F3.opExtrude","CAP_FACE",FACE,{"disambiguationData":[OSD([subQ5,subQ1,subQ6,subQ7,subQ4,subQ3,subQ2,subQ0])],"isStart":false})})}),makeQuery(id+"F8.opExtrude","SWEPT_FACE",FACE,{"disambiguationData":[OSD([sQuery(id+"F7.wireOp",EDGE,"E67")])]})]});}
            var Q5;
            Q5=makeQuery(id+"F8.boolean.opBoolean","INTERSECT",EDGE,{"disambiguationData":[OD(0.0)],"derivedFrom":[makeQuery(id+"F5.opExtrude","SWEPT_FACE",FACE,{"disambiguationData":[OSD([sQuery(id+"F4.wireOp",EDGE,"E30")])]}),makeQuery(id+"F8.opExtrude","SWEPT_FACE",FACE,{"disambiguationData":[OSD([sQuery(id+"F7.wireOp",EDGE,"E67")])]})]});
            fillet(context, id + "F14", {"entities" : qUnion([Q0, Q1, Q2, Q3, Q4, Q5]), "radius" : 3 * mm, "tangentPropagation" : true, "allowEdgeOverflow" : false});
        }
        {
            var Q0;
            Q0=makeQuery(id+"F1.opExtrude","CAP_EDGE",EDGE,{"disambiguationData":[OSD([sQuery(id+"F0.wireOp",EDGE,"E1.bottom")])],"isStart":false});
            fillet(context, id + "F15", {"entities" : qUnion([Q0]), "radius" : 2 * mm, "tangentPropagation" : true, "allowEdgeOverflow" : false});
        }
        {
            var Q0;
            {var subQ0=sQuery(id+"F0.wireOp",EDGE,"E22.filletArc");var subQ1=sQuery(id+"F0.wireOp",EDGE,"E7");var subQ2=sQuery(id+"F0.wireOp",EDGE,"E6");var subQ3=sQuery(id+"F0.wireOp",EDGE,"E5");var subQ4=sQuery(id+"F0.wireOp",EDGE,"E4");var subQ5=sQuery(id+"F0.wireOp",EDGE,"E1.bottom");var subQ6=sQuery(id+"F0.wireOp",EDGE,"E21.filletArc");var subQ7=sQuery(id+"F0.wireOp",EDGE,"E1.top");var subQ8=sQuery(id+"F0.wireOp",EDGE,"E1.left");var subQ9=sQuery(id+"F0.wireOp",EDGE,"E1.right");var subQ10=sQuery(id+"F0.wireOp",EDGE,"E23.filletArc");var subQ11=sQuery(id+"F0.wireOp",EDGE,"E24.filletArc");Q0=makeQuery(id+"F2.boolean.opBoolean","SPLIT",FACE,{"disambiguationData":[TD([makeQuery(id+"F1.opExtrude","SWEPT_FACE",FACE,{"disambiguationData":[OSD([subQ5])]})])],"derivedFrom":makeQuery(id+"F1.opExtrude","CAP_FACE",FACE,{"disambiguationData":[OSD([subQ5,subQ7,subQ8,subQ9,subQ4,subQ3,subQ2,subQ1,subQ6,subQ0,subQ10,subQ11])],"isStart":true})});}
            var sketch = newSketch(context, id + "F16", { "sketchPlane" : qUnion([Q0])});
            skLineSegment(sketch, "E79", {"start": v(0, 90) * mm, "end": v(0, 120) * mm, "construction": true});
            skCircle(sketch, "E80", {"center": v(0, 120) * mm, "radius": 6 * mm});
            skArc(sketch, "E81", {"start": v(-15, 120) * mm, "mid": v(0, 135) * mm, "end": v(15, 120) * mm});
            skLineSegment(sketch, "E82", {"start": v(-15, 120) * mm, "end": v(-15, 108) * mm});
            skLineSegment(sketch, "E83", {"start": v(-15, 108) * mm, "end": v(-33, 90) * mm});
            skLineSegment(sketch, "E84", {"start": v(15, 120) * mm, "end": v(15, 108) * mm});
            skLineSegment(sketch, "E85", {"start": v(15, 108) * mm, "end": v(33, 90) * mm});
            skLineSegment(sketch, "E86", {"start": v(-80, 0) * mm, "end": v(80, 0) * mm, "construction": true});
            skLineSegment(sketch, "E87.MirrorCS", {"start": v(0, -90) * mm, "end": v(0, -120) * mm, "construction": true});
            skCircle(sketch, "E88.MirrorC", {"center": v(0, -120) * mm, "radius": 6 * mm});
            skArc(sketch, "E89.MirrorCS", {"start": v(-15, -120) * mm, "mid": v(0, -135) * mm, "end": v(15, -120) * mm});
            skLineSegment(sketch, "E90.MirrorCS", {"start": v(-15, -120) * mm, "end": v(-15, -108) * mm});
            skLineSegment(sketch, "E91.MirrorCS", {"start": v(15, -120) * mm, "end": v(15, -108) * mm});
            skLineSegment(sketch, "E92.MirrorCS", {"start": v(-15, -108) * mm, "end": v(-33, -90) * mm});
            skLineSegment(sketch, "E93.MirrorCS", {"start": v(15, -108) * mm, "end": v(33, -90) * mm});
            skSolve(sketch);
        }
        {
            var Q0;
            Q0=makeQuery(id+"F16.imprint","IMPRINT",FACE,{"disambiguationData":[TD([[makeQuery(id+"F16.imprint","IMPRINT",EDGE,{"derivedFrom":sQuery(id+"F16.wireOp",EDGE,"E88.MirrorC")}),1.0]])]});
            var Q1;
            Q1=makeQuery(id+"F16.imprint","IMPRINT",FACE,{"disambiguationData":[TD([[makeQuery(id+"F16.imprint","IMPRINT",EDGE,{"derivedFrom":sQuery(id+"F16.wireOp",EDGE,"E80")}),-1.0]])]});
            var Q2;
            Q2=makeQuery(id+"F16.imprint","IMPRINT",FACE,{"disambiguationData":[TD([[makeQuery(id+"F16.imprint","IMPRINT",EDGE,{"derivedFrom":makeQuery(id+"F1.opExtrude","CAP_EDGE",EDGE,{"disambiguationData":[OSD([sQuery(id+"F0.wireOp",EDGE,"E1.left")])],"isStart":true})}),-1.0]])]});
            var Q3;
            Q3=makeQuery(id+"F2.opExtrude","CAP_FACE",FACE,{"disambiguationData":[OSD([sQuery(id+"F0.wireOp",EDGE,"E12"),sQuery(id+"F0.wireOp",EDGE,"E13"),sQuery(id+"F0.wireOp",EDGE,"E14"),sQuery(id+"F0.wireOp",EDGE,"E15"),sQuery(id+"F0.wireOp",EDGE,"E17.filletArc"),sQuery(id+"F0.wireOp",EDGE,"E18.filletArc"),sQuery(id+"F0.wireOp",EDGE,"E19.filletArc"),sQuery(id+"F0.wireOp",EDGE,"E20.filletArc"),sQuery(id+"F0.wireOp",EDGE,"E25.0"),sQuery(id+"F0.wireOp",EDGE,"E25.1"),sQuery(id+"F0.wireOp",EDGE,"E25.2"),sQuery(id+"F0.wireOp",EDGE,"E25.3"),sQuery(id+"F0.wireOp",EDGE,"E25.4"),sQuery(id+"F0.wireOp",EDGE,"E25.5"),sQuery(id+"F0.wireOp",EDGE,"E25.6"),sQuery(id+"F0.wireOp",EDGE,"E25.7")])],"isStart":false});
            extrude(context, id + "F17", {"entities" : qUnion([Q0, Q1, Q2]), "endBound" : BoundingType.UP_TO_SURFACE, "endBoundEntityFace" : qUnion([Q3]), "depth" : 25 * mm});
        }
    });
